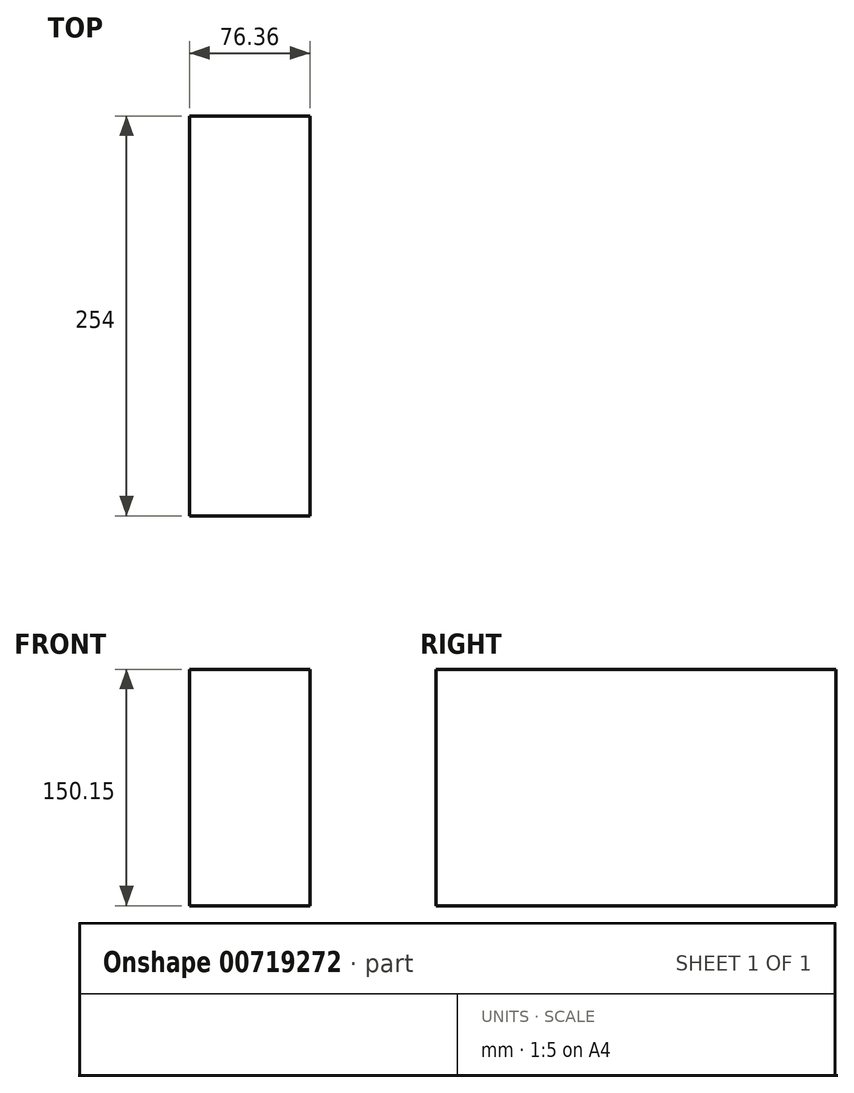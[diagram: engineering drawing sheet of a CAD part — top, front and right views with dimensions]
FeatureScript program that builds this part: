
annotation { "Feature Type Name" : "Feature", "Feature Type Description" : "" }
export const myFeature = defineFeature(function(context is Context, id is Id, definition is map)
    precondition{}
    {
        {
            var Q0;
            Q0=qCreatedBy(makeId("Front.planeOp"),FACE);
            var sketch = newSketch(context, id + "F0", { "sketchPlane" : qUnion([Q0])});
            skLineSegment(sketch, "E0.bottom", {"start": v(-27.8, -119.12) * mm, "end": v(48.56, -119.12) * mm});
            skLineSegment(sketch, "E0.top", {"start": v(-27.8, 31.03) * mm, "end": v(48.56, 31.03) * mm});
            skLineSegment(sketch, "E0.left", {"start": v(-27.8, -119.12) * mm, "end": v(-27.8, 31.03) * mm});
            skLineSegment(sketch, "E0.right", {"start": v(48.56, -119.12) * mm, "end": v(48.56, 31.03) * mm});
            skSolve(sketch);
        }
        {
            var Q0;
            Q0 = qSketchRegion(id + "F0", true);
            var Q1;
            Q1=makeQuery(id+"F0.imprint","IMPRINT",FACE,{"disambiguationData":[TD([[makeQuery(id+"F0.imprint","IMPRINT",EDGE,{"derivedFrom":sQuery(id+"F0.wireOp",EDGE,"E0.bottom")}),1.0]])]});
            extrude(context, id + "F1", {"entities" : qUnion([Q0, Q1]), "depth" : 254 * mm, "offsetDistance" : 25.4 * mm});
        }
    });
